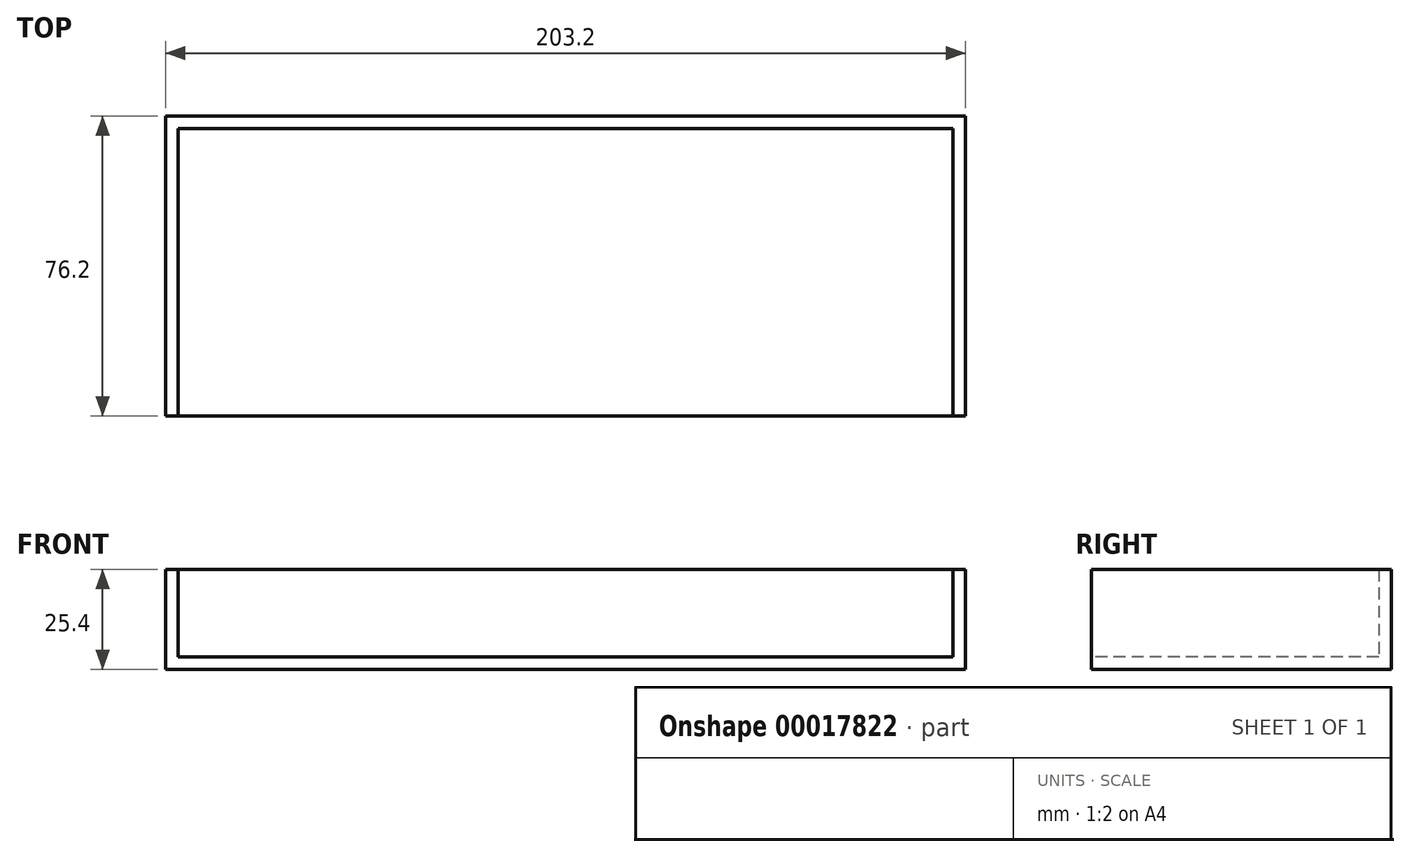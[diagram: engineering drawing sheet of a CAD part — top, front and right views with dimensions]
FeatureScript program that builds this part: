
annotation { "Feature Type Name" : "Feature", "Feature Type Description" : "" }
export const myFeature = defineFeature(function(context is Context, id is Id, definition is map)
    precondition{}
    {
        {
            var Q0;
            Q0=qCreatedBy(makeId("Top.planeOp"),FACE);
            var sketch = newSketch(context, id + "F0", { "sketchPlane" : qUnion([Q0])});
            skLineSegment(sketch, "E0.rect.bottom", {"start": v(-101.6, 38.1) * mm, "end": v(101.6, 38.1) * mm});
            skLineSegment(sketch, "E0.rect.top", {"start": v(-101.6, -38.1) * mm, "end": v(101.6, -38.1) * mm});
            skLineSegment(sketch, "E0.rect.left", {"start": v(-101.6, 38.1) * mm, "end": v(-101.6, -38.1) * mm});
            skLineSegment(sketch, "E0.rect.right", {"start": v(101.6, 38.1) * mm, "end": v(101.6, -38.1) * mm});
            skPoint(sketch, "E0.rect.middle", {"position": v(0, 0) * mm});
            skSolve(sketch);
        }
        {
            var Q0;
            Q0 = qSketchRegion(id + "F0", true);
            extrude(context, id + "F1", {"entities" : qUnion([Q0]), "endBound" : BoundingType.SYMMETRIC, "depth" : 25.4 * mm});
        }
        {
            var Q0;
            Q0=makeQuery(id+"F1.opExtrude","CAP_FACE",FACE,{"disambiguationData":[OSD([sQuery(id+"F0.wireOp",EDGE,"E0.rect.bottom"),sQuery(id+"F0.wireOp",EDGE,"E0.rect.top"),sQuery(id+"F0.wireOp",EDGE,"E0.rect.left"),sQuery(id+"F0.wireOp",EDGE,"E0.rect.right")])],"isStart":false});
            var Q1;
            Q1=makeQuery(id+"F1.opExtrude","SWEPT_FACE",FACE,{"disambiguationData":[OSD([sQuery(id+"F0.wireOp",EDGE,"E0.rect.top")])]});
            shell(context, id + "F2", {"entities" : qUnion([Q0, Q1]), "thickness" : 3.17 * mm});
        }
    });
